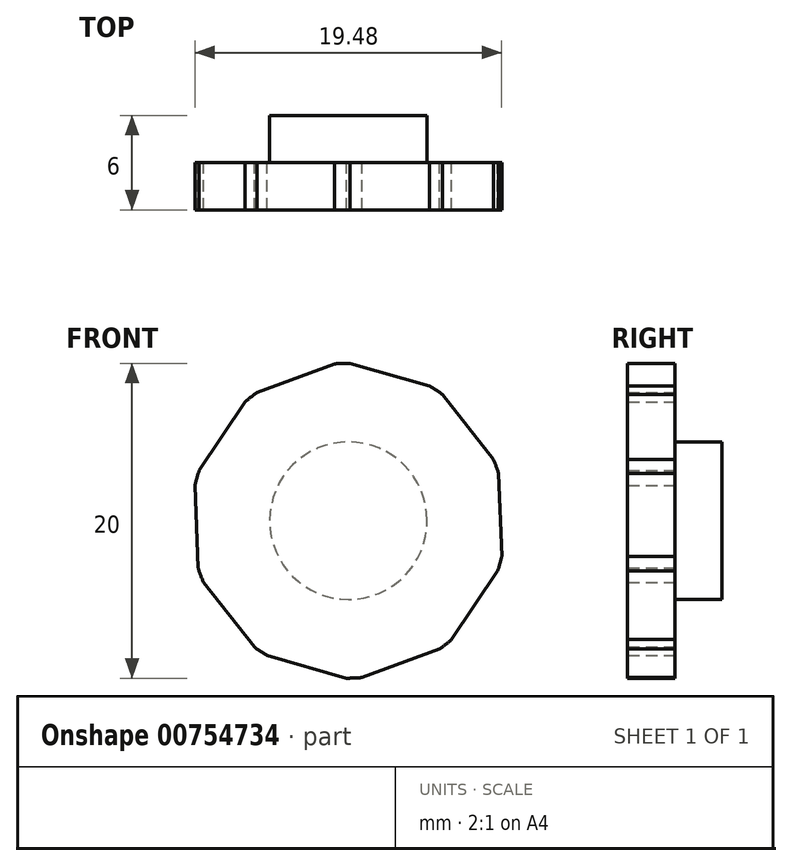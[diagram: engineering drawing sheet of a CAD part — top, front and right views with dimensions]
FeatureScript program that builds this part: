
annotation { "Feature Type Name" : "Feature", "Feature Type Description" : "" }
export const myFeature = defineFeature(function(context is Context, id is Id, definition is map)
    precondition{}
    {
        {
            var Q0;
            Q0=qCreatedBy(makeId("Front.planeOp"),FACE);
            var sketch = newSketch(context, id + "F0", { "sketchPlane" : qUnion([Q0])});
            skCircle(sketch, "E0", {"center": v(0, 0) * mm, "radius": 5 * mm});
            skSolve(sketch);
        }
        {
            var Q0;
            Q0 = qSketchRegion(id + "F0", true);
            extrude(context, id + "F1", {"entities" : qUnion([Q0]), "depth" : 3 * mm, "offsetDistance" : 25 * mm});
        }
        {
            var Q0;
            Q0=makeQuery(id+"F1.opExtrude","CAP_FACE",FACE,{"disambiguationData":[OSD([sQuery(id+"F0.wireOp",EDGE,"E0")])],"isStart":false});
            var sketch = newSketch(context, id + "F2", { "sketchPlane" : qUnion([Q0])});
            skCircle(sketch, "E1", {"center": v(0, 0) * mm, "radius": 10 * mm});
            skSolve(sketch);
        }
        {
            var Q0;
            Q0 = qSketchRegion(id + "F2", true);
            extrude(context, id + "F3", {"entities" : qUnion([Q0]), "operationType" : NewBodyOperationType.ADD, "depth" : 3 * mm, "offsetDistance" : 25 * mm});
        }
        {
            var Q0;
            Q0=makeQuery(id+"F3.opExtrude","CAP_FACE",FACE,{"disambiguationData":[OSD([sQuery(id+"F2.wireOp",EDGE,"E1")])],"isStart":false});
            var sketch = newSketch(context, id + "F4", { "sketchPlane" : qUnion([Q0])});
            skCircle(sketch, "E2.cCircle", {"center": v(0, 0) * mm, "radius": 9.65 * mm, "construction": true});
            skLineSegment(sketch, "E2.0", {"start": v(-0.39, 10.14) * mm, "end": v(5.65, 8.43) * mm});
            skLineSegment(sketch, "E2.1", {"start": v(5.65, 8.43) * mm, "end": v(9.52, 3.5) * mm});
            skLineSegment(sketch, "E2.2", {"start": v(9.52, 3.5) * mm, "end": v(9.76, -2.77) * mm});
            skLineSegment(sketch, "E2.3", {"start": v(9.76, -2.77) * mm, "end": v(6.27, -7.98) * mm});
            skLineSegment(sketch, "E2.4", {"start": v(6.27, -7.98) * mm, "end": v(0.39, -10.14) * mm});
            skLineSegment(sketch, "E2.5", {"start": v(0.39, -10.14) * mm, "end": v(-5.65, -8.43) * mm});
            skLineSegment(sketch, "E2.6", {"start": v(-5.65, -8.43) * mm, "end": v(-9.52, -3.5) * mm});
            skLineSegment(sketch, "E2.7", {"start": v(-9.52, -3.5) * mm, "end": v(-9.76, 2.77) * mm});
            skLineSegment(sketch, "E2.8", {"start": v(-9.76, 2.77) * mm, "end": v(-6.27, 7.98) * mm});
            skLineSegment(sketch, "E2.9", {"start": v(-6.27, 7.98) * mm, "end": v(-0.39, 10.14) * mm});
            skPoint(sketch, "E2.0.midPoint", {"position": v(2.63, 9.28) * mm});
            skCircle(sketch, "E3", {"center": v(0, 0) * mm, "radius": 11.27 * mm});
            skSolve(sketch);
        }
        {
            var Q0;
            Q0 = qSketchRegion(id + "F4", true);
            extrude(context, id + "F5", {"entities" : qUnion([Q0]), "operationType" : NewBodyOperationType.REMOVE, "oppositeDirection" : true, "depth" : 25 * mm, "offsetDistance" : 25 * mm});
        }
    });
